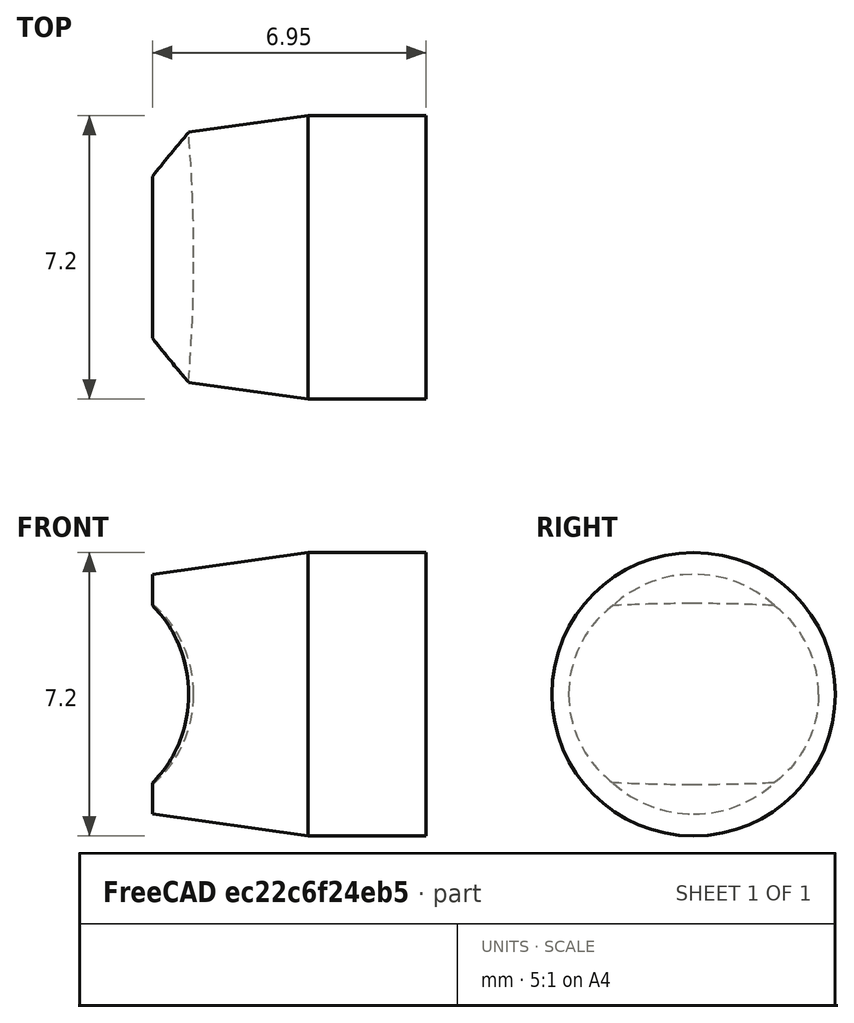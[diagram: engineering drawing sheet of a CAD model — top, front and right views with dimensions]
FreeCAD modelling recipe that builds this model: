
FCSTD DOCUMENT  (FreeCAD 0.16R6703 (Git))
Label: Art4BearingPlug
License: All rights reserved
LicenseURL: http://en.wikipedia.org/wiki/All_rights_reserved
objects: Part::Torus×1, Part::Cone×1, Part::Cylinder×1, Part::MultiFuse×1, Part::Cut×1, Part::Box×1, Part::MultiCommon×1
note: 7 computed .brp shape members not serialized (recipe doc carries the construction recipe); baked Part::Feature solids carry a one-line shape summary decoded from their .brp

FEATURE [Part::Torus] Torus020  label="Torus"
  Angle1 = -180
  Angle2 = 180
  Angle3 = 360
  Placement = pos=(0,0,1) rot=(0,0,1;0rad)
  Radius1 = 35
  Radius2 = 3.05
FEATURE [Part::Cone] Cone003  label="Cone"
  Angle = 360
  Height = 5
  Placement = pos=(34.95,0,0) rot=(0,1,0;1.5708rad)
  Radius1 = 2.9
  Radius2 = 3.6
FEATURE [Part::Cylinder] Cylinder801  label="Cylinder"
  Angle = 360
  Height = 3
  Placement = pos=(39.95,0,0) rot=(0,1,0;1.5708rad)
  Radius = 3.6
FEATURE [Part::MultiFuse] Fusion611  label="Fusion"
  Placement = pos=(1,0,1) rot=(0,0,1;0rad)
  Shapes = -> [Cylinder801,Cone003]
FEATURE [Part::Cut] Cut066379  label="Cut"
  Base = -> Fusion611
  Tool = -> Torus020
FEATURE [Part::Box] Box179  label="Cube"
  Height = 10
  Length = 16
  Placement = pos=(37,-5,-3) rot=(0,0,1;0rad)
  Width = 10
FEATURE [Part::MultiCommon] Common053  label="Art4BearingPlug"
  Placement = pos=(0,0,-1) rot=(0,0,1;0rad)
  Shapes = -> [Box179,Cut066379]
